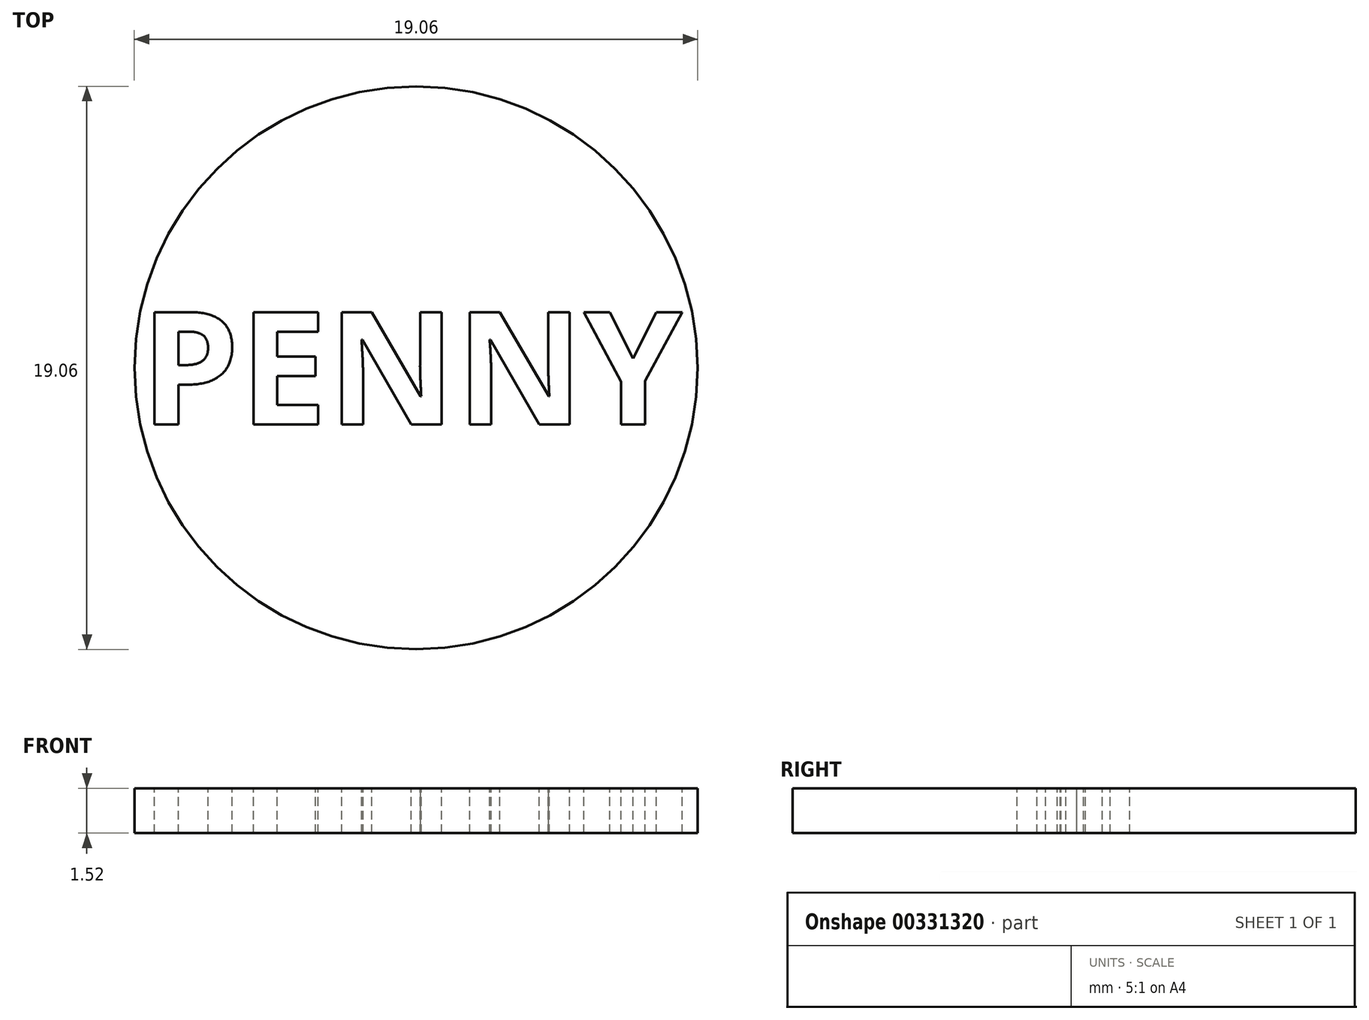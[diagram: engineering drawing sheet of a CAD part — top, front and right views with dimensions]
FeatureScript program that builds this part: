
annotation { "Feature Type Name" : "Feature", "Feature Type Description" : "" }
export const myFeature = defineFeature(function(context is Context, id is Id, definition is map)
    precondition{}
    {
        {
            var Q0;
            Q0=qCreatedBy(makeId("Top.planeOp"),FACE);
            var sketch = newSketch(context, id + "F0", { "sketchPlane" : qUnion([Q0])});
            skCircle(sketch, "E0", {"center": v(0, 0) * mm, "radius": 9.53 * mm});
            skSolve(sketch);
        }
        {
            var Q0;
            Q0=makeQuery(id+"F0.imprint","IMPRINT",FACE,{"disambiguationData":[TD([[makeQuery(id+"F0.imprint","IMPRINT",EDGE,{"derivedFrom":sQuery(id+"F0.wireOp",EDGE,"E0")}),1.0]])]});
            extrude(context, id + "F1", {"entities" : qUnion([Q0]), "depth" : 1.52 * mm, "offsetDistance" : 25 * mm});
        }
        {
            var Q0;
            Q0=makeQuery(id+"F1.opExtrude","CAP_FACE",FACE,{"disambiguationData":[OSD([sQuery(id+"F0.wireOp",EDGE,"E0")])],"isStart":false});
            var sketch = newSketch(context, id + "F2", { "sketchPlane" : qUnion([Q0])});
            skText(sketch, "E1", { "text": "PENNY", "fontName": "OpenSans-Bold.ttf"});
            const initialGuessF2  = {"E1": [-0.00933, -0.00192, 1, 0, 0.00384]};
            skSetInitialGuess(sketch, initialGuessF2);
            skSolve(sketch);
        }
        {
            var Q0;
            Q0=makeQuery(id+"F2.imprint","IMPRINT",FACE,{"disambiguationData":[TD([[makeQuery(id+"F2.imprint","IMPRINT",EDGE,{"derivedFrom":sQuery(id+"F2.wireOp",EDGE,"E1.sketch_text.stroke-16")}),-1.0]])]});
            var Q1;
            Q1=makeQuery(id+"F2.imprint","IMPRINT",FACE,{"disambiguationData":[TD([[makeQuery(id+"F2.imprint","IMPRINT",EDGE,{"derivedFrom":sQuery(id+"F2.wireOp",EDGE,"E1.sketch_text.stroke-0")}),-1.0]])]});
            var Q2;
            Q2=makeQuery(id+"F2.imprint","IMPRINT",FACE,{"disambiguationData":[TD([[makeQuery(id+"F2.imprint","IMPRINT",EDGE,{"derivedFrom":sQuery(id+"F2.wireOp",EDGE,"E1.sketch_text.stroke-28")}),-1.0]])]});
            var Q3;
            Q3=makeQuery(id+"F2.imprint","IMPRINT",FACE,{"disambiguationData":[TD([[makeQuery(id+"F2.imprint","IMPRINT",EDGE,{"derivedFrom":sQuery(id+"F2.wireOp",EDGE,"E1.sketch_text.stroke-42")}),-1.0]])]});
            var Q4;
            Q4=makeQuery(id+"F2.imprint","IMPRINT",FACE,{"disambiguationData":[TD([[makeQuery(id+"F2.imprint","IMPRINT",EDGE,{"derivedFrom":sQuery(id+"F2.wireOp",EDGE,"E1.sketch_text.stroke-56")}),-1.0]])]});
            extrude(context, id + "F3", {"entities" : qUnion([Q0, Q1, Q2, Q3, Q4]), "operationType" : NewBodyOperationType.REMOVE, "oppositeDirection" : true, "depth" : 25 * mm, "offsetDistance" : 25 * mm});
        }
    });
